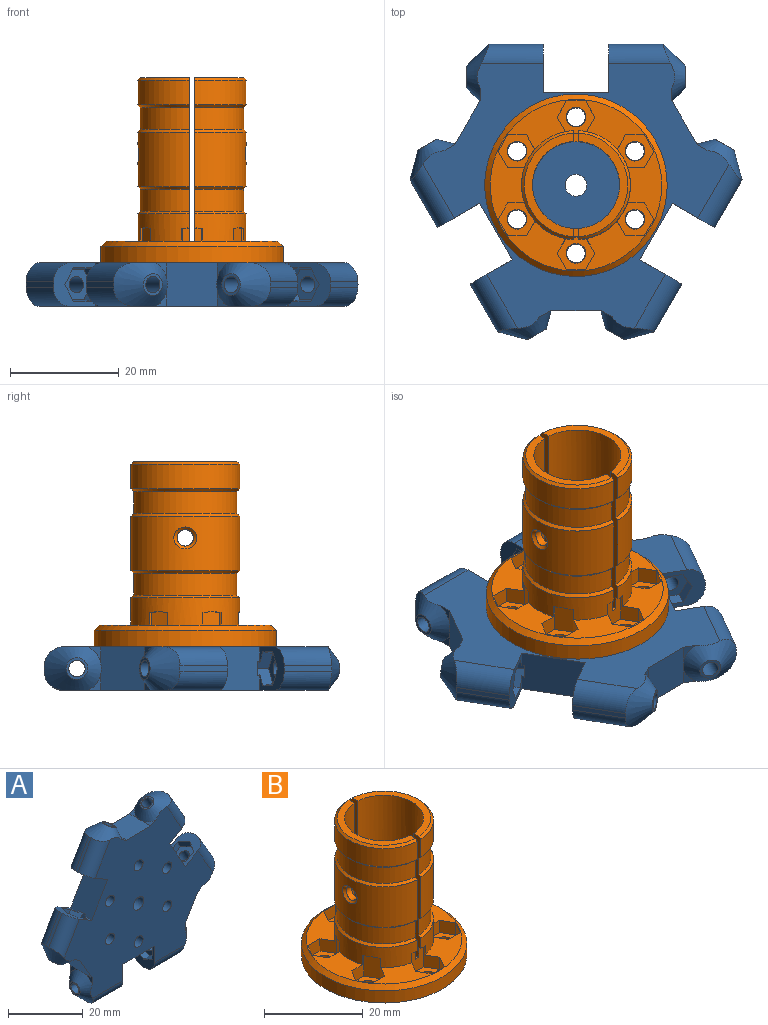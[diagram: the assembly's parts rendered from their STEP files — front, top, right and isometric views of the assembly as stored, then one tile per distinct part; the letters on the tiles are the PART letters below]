
ASSEMBLY  parts=2 mates=1
PART A: 119 faces, bbox 62.3x12.1x54.3 mm
  f0: cylinder r=2mm len=4mm, axis (0,-1,0), area 50.3mm2, adj f93,f118
  f1: cylinder r=1.7mm len=8mm, axis (0,-1,0), area 85.5mm2, adj f92,f118
  f2: cylinder r=1.7mm len=8mm, axis (0,-1,0), area 85.5mm2, adj f92,f118
  f3: cylinder r=1.7mm len=8mm, axis (0,-1,0), area 85.5mm2, adj f92,f118
  f4: cylinder r=1.7mm len=8mm, axis (0,-1,0), area 85.5mm2, adj f92,f118
  f5: cylinder r=1.7mm len=8mm, axis (0,-1,0), area 85.5mm2, adj f92,f118
  f6: cylinder r=1.7mm len=8mm, axis (0,-1,0), area 85.5mm2, adj f92,f118
  f7: cone r=6.1mm half-angle=45deg, axis (-0.5,0,-0.87), area 85.6mm2, adj f82,f83,f84,f86,f92,f114,f115,f116
  f8: cone r=6.07mm half-angle=45deg, axis (0.5,0,-0.87), area 85.6mm2, adj f78,f79,f80,f81,f92,f112,f113,f114
  f9: cone r=6.1mm half-angle=45deg, axis (-0.5,0,0.87), area 85.6mm2, adj f60,f61,f62,f64,f92,f106,f107,f108
  f10: cone r=6.07mm half-angle=45deg, axis (-1,0,0), area 85.6mm2, adj f56,f57,f58,f59,f92,f104,f105,f106
  f11: cone r=6.1mm half-angle=45deg, axis (1,0,0), area 85.6mm2, adj f37,f39,f40,f42,f92,f98,f99,f100
  f12: cone r=6.07mm half-angle=45deg, axis (0.5,0,0.87), area 85.6mm2, adj f34,f35,f36,f38,f92,f96,f97,f98
  f13: cylinder r=8mm len=16mm, axis (0,1,0), area 201.1mm2, adj f92,f93
  f14: cylinder r=1.5mm len=11.98mm, axis (-0.5,0,-0.87), area 114mm2, adj f25,f83
  f15: cylinder r=1.5mm len=11.98mm, axis (0.5,0,-0.87), area 114mm2, adj f24,f80
  f16: cylinder r=1.5mm len=11.98mm, axis (-0.5,0,0.87), area 114mm2, adj f23,f61
  f17: cylinder r=1.5mm len=12.1mm, axis (-1,0,0), area 114mm2, adj f22,f58
  f18: cylinder r=1.5mm len=12.1mm, axis (1,0,0), area 114mm2, adj f21,f39
  f19: cylinder r=1.5mm len=11.98mm, axis (0.5,0,0.87), area 114mm2, adj f20,f36
  f20: plane 5.5x5.5mm, normal (0.5,0,0.87), area 19.1mm2, adj f19,f28,f29,f30,f31,f32,f33
  f21: plane 6.35x5.5mm, normal (1,0,0), area 19.1mm2, adj f18,f41,f43,f44,f45,f46,f47
  f22: plane 6.35x5.5mm, normal (-1,0,0), area 19.1mm2, adj f17,f50,f51,f52,f53,f54,f55
  f23: plane 5.5x5.5mm, normal (-0.5,0,0.87), area 19.1mm2, adj f16,f63,f65,f66,f67,f68,f69
  f24: plane 5.5x5.5mm, normal (0.5,0,-0.87), area 19.1mm2, adj f15,f72,f73,f74,f75,f76,f77
  f25: plane 5.5x5.5mm, normal (-0.5,0,-0.87), area 19.1mm2, adj f14,f85,f87,f88,f89,f90,f91
  f26: plane 2.65x0.66mm, normal (0.5,0,0.87), area 1mm2, adj f85,f87,f94
  f27: plane 2.65x0.66mm, normal (-0.5,0,-0.87), area 1mm2, adj f28,f33,f94
  f28: plane 3.1x3.07mm, normal (-0.65,0.49,0.58), area 7.6mm2, adj f20,f27,f29,f33,f94,f95
  f29: plane 3.93x3.42mm, normal (0.09,0.98,0.15), area 6.9mm2, adj f20,f28,f30,f95
  f30: plane 3.1x2.73mm, normal (0.83,0.49,-0.28), area 6.9mm2, adj f20,f29,f31,f95
  f31: plane 3.1x2.73mm, normal (0.83,-0.49,-0.28), area 6.9mm2, adj f20,f30,f32,f95
  f32: plane 3.93x3.42mm, normal (0.09,-0.98,0.15), area 6.9mm2, adj f20,f31,f33,f95
  f33: plane 3.1x3.07mm, normal (-0.65,-0.49,0.58), area 7.6mm2, adj f20,f27,f28,f32,f94,f95
  f34: cylinder r=3.5mm len=11.61mm, axis (-0.5,0,-0.87), area 59mm2, adj f12,f35,f92,f95
  f35: plane 8.76x5.06mm, normal (-0.87,0,0.5), area 10.1mm2, adj f12,f34,f95,f96
  f36: plane 4x3.46mm, normal (-0.5,0,-0.87), area 5.5mm2, adj f12,f19
  f37: plane 2.9x2.3mm, normal (-1,0,0), area 2.3mm2, adj f11,f92,f98
  f38: plane 2.9x1.99mm, normal (-0.5,0,-0.87), area 2.3mm2, adj f12,f92,f98
  f39: plane 4x4mm, normal (-1,0,0), area 5.5mm2, adj f11,f18
  f40: plane 10.11x1.01mm, normal (0,0,-1), area 10.1mm2, adj f11,f42,f100,f101
  f41: plane 3.1x2.5mm, normal (0.17,0.49,-0.85), area 7.6mm2, adj f21,f43,f47,f48,f101,f102
  f42: cylinder r=3.5mm len=11.38mm, axis (1,0,0), area 59mm2, adj f11,f40,f92,f101
  f43: plane 3.1x2.5mm, normal (0.17,-0.49,-0.85), area 7.6mm2, adj f21,f41,f44,f48,f101,f102
  f44: plane 3.58x2mm, normal (0.17,-0.98,0), area 6.9mm2, adj f21,f43,f45,f101
  f45: plane 3.1x2mm, normal (0.17,-0.49,0.85), area 6.9mm2, adj f21,f44,f46,f101
  f46: plane 3.1x2mm, normal (0.17,0.49,0.85), area 6.9mm2, adj f21,f45,f47,f101
  f47: plane 3.58x2mm, normal (0.17,0.98,0), area 6.9mm2, adj f21,f41,f46,f101
  f48: plane 2.65x0.76mm, normal (-1,0,0), area 1mm2, adj f41,f43,f102
  f49: plane 2.65x0.76mm, normal (1,0,0), area 1mm2, adj f50,f55,f102
  f50: plane 3.1x2.5mm, normal (-0.17,0.49,-0.85), area 7.6mm2, adj f22,f49,f51,f55,f102,f103
  f51: plane 3.58x2mm, normal (-0.17,0.98,0), area 6.9mm2, adj f22,f50,f52,f103
  f52: plane 3.1x2mm, normal (-0.17,0.49,0.85), area 6.9mm2, adj f22,f51,f53,f103
  f53: plane 3.1x2mm, normal (-0.17,-0.49,0.85), area 6.9mm2, adj f22,f52,f54,f103
  f54: plane 3.58x2mm, normal (-0.17,-0.98,0), area 6.9mm2, adj f22,f53,f55,f103
  f55: plane 3.1x2.5mm, normal (-0.17,-0.49,-0.85), area 7.6mm2, adj f22,f49,f50,f54,f102,f103
  f56: cylinder r=3.5mm len=11.38mm, axis (1,0,0), area 59mm2, adj f10,f57,f92,f103
  f57: plane 10.11x1.01mm, normal (0,0,-1), area 10.1mm2, adj f10,f56,f103,f104
  f58: plane 4x4mm, normal (1,0,0), area 5.5mm2, adj f10,f17
  f59: plane 2.9x2.3mm, normal (1,0,0), area 2.3mm2, adj f10,f92,f106
  f60: plane 2.9x1.99mm, normal (0.5,0,-0.87), area 2.3mm2, adj f9,f92,f106
  f61: plane 4x3.46mm, normal (0.5,0,-0.87), area 5.5mm2, adj f9,f16
  f62: plane 8.76x5.06mm, normal (0.87,0,0.5), area 10.1mm2, adj f9,f64,f108,f109
  f63: plane 3.1x3.07mm, normal (0.65,0.49,0.58), area 7.6mm2, adj f23,f65,f69,f70,f109,f110
  f64: cylinder r=3.5mm len=11.61mm, axis (-0.5,0,0.87), area 59mm2, adj f9,f62,f92,f109
  f65: plane 3.1x3.07mm, normal (0.65,-0.49,0.58), area 7.6mm2, adj f23,f63,f66,f70,f109,f110
  f66: plane 3.93x3.42mm, normal (-0.09,-0.98,0.15), area 6.9mm2, adj f23,f65,f67,f109
  f67: plane 3.1x2.73mm, normal (-0.83,-0.49,-0.28), area 6.9mm2, adj f23,f66,f68,f109
  f68: plane 3.1x2.73mm, normal (-0.83,0.49,-0.28), area 6.9mm2, adj f23,f67,f69,f109
  f69: plane 3.93x3.42mm, normal (-0.09,0.98,0.15), area 6.9mm2, adj f23,f63,f68,f109
  f70: plane 2.65x0.66mm, normal (0.5,0,-0.87), area 1mm2, adj f63,f65,f110
  f71: plane 2.65x0.66mm, normal (-0.5,0,0.87), area 1mm2, adj f72,f77,f110
  f72: plane 3.21x3.1mm, normal (0.83,0.49,0.28), area 7.6mm2, adj f24,f71,f73,f77,f110,f111
  f73: plane 3.93x3.42mm, normal (0.09,0.98,-0.15), area 6.9mm2, adj f24,f72,f74,f111
  f74: plane 3.1x2.73mm, normal (-0.65,0.49,-0.58), area 6.9mm2, adj f24,f73,f75,f111
  f75: plane 3.1x2.73mm, normal (-0.65,-0.49,-0.58), area 6.9mm2, adj f24,f74,f76,f111
  f76: plane 3.93x3.42mm, normal (0.09,-0.98,-0.15), area 6.9mm2, adj f24,f75,f77,f111
  f77: plane 3.21x3.1mm, normal (0.83,-0.49,0.28), area 7.6mm2, adj f24,f71,f72,f76,f110,f111
  f78: cylinder r=3.5mm len=11.61mm, axis (-0.5,0,0.87), area 59mm2, adj f8,f79,f92,f111
  f79: plane 8.76x5.06mm, normal (0.87,0,0.5), area 10.1mm2, adj f8,f78,f111,f112
  f80: plane 4x3.46mm, normal (-0.5,0,0.87), area 5.5mm2, adj f8,f15
  f81: plane 2.9x1.99mm, normal (-0.5,0,0.87), area 2.3mm2, adj f8,f92,f114
  f82: plane 2.9x1.99mm, normal (0.5,0,0.87), area 2.3mm2, adj f7,f92,f114
  f83: plane 4x3.46mm, normal (0.5,0,0.87), area 5.5mm2, adj f7,f14
  f84: plane 8.76x5.06mm, normal (-0.87,0,0.5), area 10.1mm2, adj f7,f86,f116,f117
  f85: plane 3.21x3.1mm, normal (-0.83,0.49,0.28), area 7.6mm2, adj f25,f26,f87,f91,f94,f117
  f86: cylinder r=3.5mm len=11.61mm, axis (-0.5,0,-0.87), area 59mm2, adj f7,f84,f92,f117
  f87: plane 3.21x3.1mm, normal (-0.83,-0.49,0.28), area 7.6mm2, adj f25,f26,f85,f88,f94,f117
  f88: plane 3.93x3.42mm, normal (-0.09,-0.98,-0.15), area 6.9mm2, adj f25,f87,f89,f117
  f89: plane 3.1x2.73mm, normal (0.65,-0.49,-0.58), area 6.9mm2, adj f25,f88,f90,f117
  f90: plane 3.1x2.73mm, normal (0.65,0.49,-0.58), area 6.9mm2, adj f25,f89,f91,f117
  f91: plane 3.93x3.42mm, normal (-0.09,0.98,-0.15), area 6.9mm2, adj f25,f85,f90,f117
  f92: plane 56.17x48.64mm, normal (0,1,0), area 1422.3mm2, adj f1,f2,f3,f4,f5,f6,f7,f8
  f93: plane 16x16mm, normal (0,1,0), area 188.5mm2, adj f0,f13
  f94: plane 10.39x8mm, normal (-0.87,0,0.5), area 93.5mm2, adj f26,f27,f28,f33,f85,f87,f92,f95
  f95: plane 8x7.73mm, normal (0.5,0,0.87), area 33.5mm2, adj f28,f29,f30,f31,f32,f33,f34,f35
  f96: cylinder r=3.5mm len=11.61mm, axis (-0.5,0,-0.87), area 59mm2, adj f12,f35,f95,f118
  f97: plane 2.9x1.99mm, normal (-0.5,0,-0.87), area 2.3mm2, adj f12,f98,f118
  f98: plane 8.09x8.04mm, normal (-0.87,0,-0.5), area 74.1mm2, adj f11,f12,f37,f38,f92,f97,f99,f118
  f99: plane 2.9x2.3mm, normal (-1,0,0), area 2.3mm2, adj f11,f98,f118
  f100: cylinder r=3.5mm len=11.38mm, axis (1,0,0), area 59mm2, adj f11,f40,f101,f118
  f101: plane 8.92x8mm, normal (1,0,0), area 33.5mm2, adj f40,f41,f42,f43,f44,f45,f46,f47
  f102: plane 12x8mm, normal (0,0,-1), area 93.5mm2, adj f41,f43,f48,f49,f50,f55,f92,f101
  f103: plane 8.92x8mm, normal (-1,0,0), area 33.5mm2, adj f50,f51,f52,f53,f54,f55,f56,f57
  f104: cylinder r=3.5mm len=11.38mm, axis (1,0,0), area 59mm2, adj f10,f57,f103,f118
  f105: plane 2.9x2.3mm, normal (1,0,0), area 2.3mm2, adj f10,f106,f118
  f106: plane 8.09x8.04mm, normal (0.87,0,-0.5), area 74.1mm2, adj f9,f10,f59,f60,f92,f105,f107,f118
  f107: plane 2.9x1.99mm, normal (0.5,0,-0.87), area 2.3mm2, adj f9,f106,f118
  f108: cylinder r=3.5mm len=11.61mm, axis (-0.5,0,0.87), area 59mm2, adj f9,f62,f109,f118
  f109: plane 8x7.73mm, normal (-0.5,0,0.87), area 33.5mm2, adj f62,f63,f64,f65,f66,f67,f68,f69
  f110: plane 10.39x8mm, normal (0.87,0,0.5), area 93.5mm2, adj f63,f65,f70,f71,f72,f77,f92,f109
  f111: plane 8x7.73mm, normal (0.5,0,-0.87), area 33.5mm2, adj f72,f73,f74,f75,f76,f77,f78,f79
  f112: cylinder r=3.5mm len=11.61mm, axis (-0.5,0,0.87), area 59mm2, adj f8,f79,f111,f118
  f113: plane 2.9x1.99mm, normal (-0.5,0,0.87), area 2.3mm2, adj f8,f114,f118
  f114: plane 9.33x8.04mm, normal (0,0,1), area 74.1mm2, adj f7,f8,f81,f82,f92,f113,f115,f118
  f115: plane 2.9x1.99mm, normal (0.5,0,0.87), area 2.3mm2, adj f7,f114,f118
  f116: cylinder r=3.5mm len=11.61mm, axis (-0.5,0,-0.87), area 59mm2, adj f7,f84,f117,f118
  f117: plane 8x7.73mm, normal (-0.5,0,-0.87), area 33.5mm2, adj f84,f85,f86,f87,f88,f89,f90,f91
  f118: plane 56.17x48.64mm, normal (0,-1,0), area 1610.8mm2, adj f0,f1,f2,f3,f4,f5,f6,f7
PART B: 105 faces, bbox 33.5x33.5x34 mm
  f0: cylinder r=8mm len=34mm, axis (0,0,1), area 1634.8mm2, adj f6,f7,f8,f11,f12,f14,f16,f25
  f1: cylinder r=10mm len=19.98mm, axis (0,0,-1), area 290.9mm2, adj f8,f11,f29,f31,f94
  f2: cylinder r=10mm len=19.98mm, axis (0,0,-1), area 290.9mm2, adj f7,f12,f33,f37,f93
  f3: plane 31.5x31.5mm, normal (0,0,1), area 287.8mm2, adj f4,f5,f17,f18,f19,f21,f22,f39
  f4: cylinder r=10mm len=19.98mm, axis (0,0,-1), area 130.3mm2, adj f3,f8,f11,f13,f32,f56,f62,f64
  f5: cylinder r=10mm len=19.98mm, axis (0,0,-1), area 130.3mm2, adj f3,f7,f12,f24,f36,f39,f40,f46
  f6: plane 1.52x1mm, normal (0,0,1), area 1.5mm2, adj f0,f7,f8,f57
  f7: plane 30x2mm, normal (1,0,0), area 54.2mm2, adj f0,f2,f5,f6,f9,f14,f33,f34
  f8: plane 30x2mm, normal (-1,0,0), area 54.2mm2, adj f0,f1,f4,f6,f10,f25,f27,f28
  f9: cylinder r=10mm len=19.98mm, axis (0,0,-1), area 136.9mm2, adj f7,f12,f34,f95
  f10: cylinder r=10mm len=19.98mm, axis (0,0,-1), area 136.9mm2, adj f8,f11,f28,f96
  f11: plane 30x2mm, normal (-1,0,0), area 55.3mm2, adj f0,f1,f4,f10,f13,f25,f26,f27
  f12: plane 30x2mm, normal (1,0,0), area 55.3mm2, adj f0,f2,f5,f9,f14,f24,f26,f33
  f13: plane 1.41x0.49mm, normal (0,0,-1), area 0.6mm2, adj f4,f11,f20,f21
  f14: plane 18.97x9mm, normal (0,0,1), area 39.7mm2, adj f0,f7,f12,f95
  f15: cylinder r=16.75mm len=33.5mm, axis (0,0,-1), area 315.7mm2, adj f16,f90
  f16: plane 33.5x33.5mm, normal (0,0,-1), area 619.3mm2, adj f0,f15,f74,f75,f76,f77,f78,f79
  f17: plane 3.46x3mm, normal (0,-1,0), area 10.4mm2, adj f3,f18,f22,f23
  f18: plane 3x3mm, normal (0.87,-0.5,0), area 10.4mm2, adj f3,f17,f19,f23
  f19: plane 3x3mm, normal (0.87,0.5,0), area 10.4mm2, adj f3,f18,f20,f23,f24
  f20: plane 3.46x3mm, normal (0,1,0), area 10.4mm2, adj f13,f19,f21,f23,f24,f26
  f21: plane 3x3mm, normal (-0.87,0.5,0), area 10.4mm2, adj f3,f13,f20,f22,f23
  f22: plane 3x3mm, normal (-0.87,-0.5,0), area 10.4mm2, adj f3,f17,f21,f23
  f23: plane 6.93x6mm, normal (0,0,1), area 21mm2, adj f17,f18,f19,f20,f21,f22,f79
  f24: plane 1.41x0.49mm, normal (0,0,-1), area 0.6mm2, adj f5,f12,f19,f20
  f25: plane 18.97x9mm, normal (0,0,1), area 39.7mm2, adj f0,f8,f11,f96
  f26: plane 1.52x1mm, normal (0,0,1), area 1.5mm2, adj f0,f11,f12,f20
  f27: cylinder r=9.49mm len=18.95mm, axis (0,0,1), area 115.2mm2, adj f8,f11,f102,f103
  f28: plane 19.98x9.5mm, normal (0,0,-1), area 0.4mm2, adj f8,f10,f11,f102
  f29: plane 19.98x9.5mm, normal (0,0,1), area 0.4mm2, adj f1,f8,f11,f103
  f30: cylinder r=9.49mm len=18.95mm, axis (0,0,1), area 115.2mm2, adj f8,f11,f99,f100
  f31: plane 19.98x9.5mm, normal (0,0,-1), area 0.4mm2, adj f1,f8,f11,f99
  f32: plane 19.98x9.5mm, normal (0,0,1), area 0.4mm2, adj f4,f8,f11,f100
  f33: plane 19.98x9.5mm, normal (0,0,1), area 0.4mm2, adj f2,f7,f12,f104
  f34: plane 19.98x9.5mm, normal (0,0,-1), area 0.4mm2, adj f7,f9,f12,f101
  f35: cylinder r=9.49mm len=18.95mm, axis (0,0,1), area 115.2mm2, adj f7,f12,f101,f104
  f36: plane 19.98x9.5mm, normal (0,0,1), area 0.4mm2, adj f5,f7,f12,f97
  f37: plane 19.98x9.5mm, normal (0,0,-1), area 0.4mm2, adj f2,f7,f12,f98
  f38: cylinder r=9.49mm len=18.95mm, axis (0,0,1), area 115.2mm2, adj f7,f12,f97,f98
  f39: plane 5.3x3.46mm, normal (0,1,0), area 11.2mm2, adj f3,f5,f42,f43,f45,f80
  f40: plane 5.3x3mm, normal (-0.87,-0.5,0), area 11.2mm2, adj f3,f5,f43,f44,f45,f81
  f41: plane 3x3mm, normal (0.87,-0.5,0), area 10.4mm2, adj f3,f42,f44,f45
  f42: plane 3x3mm, normal (0.87,0.5,0), area 10.4mm2, adj f3,f39,f41,f45
  f43: plane 5.45x3mm, normal (-0.87,0.5,0), area 18.6mm2, adj f39,f40,f45,f80,f81
  f44: plane 3.46x3mm, normal (0,-1,0), area 10.4mm2, adj f3,f40,f41,f45
  f45: plane 6.93x6mm, normal (0,0,1), area 21mm2, adj f39,f40,f41,f42,f43,f44,f78
  f46: plane 5.3x3mm, normal (-0.87,0.5,0), area 11.2mm2, adj f3,f5,f49,f50,f52,f82
  f47: plane 5.3x3.46mm, normal (0,-1,0), area 11.2mm2, adj f3,f5,f50,f51,f52,f83
  f48: plane 3x3mm, normal (0.87,0.5,0), area 10.4mm2, adj f3,f49,f51,f52
  f49: plane 3.46x3mm, normal (0,1,0), area 10.4mm2, adj f3,f46,f48,f52
  f50: plane 5.45x3mm, normal (-0.87,-0.5,0), area 18.6mm2, adj f46,f47,f52,f82,f83
  f51: plane 3x3mm, normal (0.87,-0.5,0), area 10.4mm2, adj f3,f47,f48,f52
  f52: plane 6.93x6mm, normal (0,0,1), area 21mm2, adj f46,f47,f48,f49,f50,f51,f77
  f53: plane 5.3x3mm, normal (0.87,-0.5,0), area 11.2mm2, adj f3,f5,f57,f58,f59,f84
  f54: plane 3.46x3mm, normal (0,1,0), area 10.4mm2, adj f3,f55,f58,f59
  f55: plane 3x3mm, normal (-0.87,0.5,0), area 10.4mm2, adj f3,f54,f56,f59
  f56: plane 5.3x3mm, normal (-0.87,-0.5,0), area 11.2mm2, adj f3,f4,f55,f57,f59,f85
  f57: plane 5.41x3.46mm, normal (0,-1,0), area 16.2mm2, adj f6,f7,f8,f53,f56,f59,f84,f85
  f58: plane 3x3mm, normal (0.87,0.5,0), area 10.4mm2, adj f3,f53,f54,f59
  f59: plane 6.93x6mm, normal (0,0,1), area 21mm2, adj f53,f54,f55,f56,f57,f58,f76
  f60: plane 3x3mm, normal (-0.87,0.5,0), area 10.4mm2, adj f3,f61,f65,f66
  f61: plane 3x3mm, normal (-0.87,-0.5,0), area 10.4mm2, adj f3,f60,f62,f66
  f62: plane 5.3x3.46mm, normal (0,-1,0), area 11.2mm2, adj f3,f4,f61,f63,f66,f86
  f63: plane 5.45x3mm, normal (0.87,-0.5,0), area 18.6mm2, adj f62,f64,f66,f86,f87
  f64: plane 5.3x3mm, normal (0.87,0.5,0), area 11.2mm2, adj f3,f4,f63,f65,f66,f87
  f65: plane 3.46x3mm, normal (0,1,0), area 10.4mm2, adj f3,f60,f64,f66
  f66: plane 6.93x6mm, normal (0,0,1), area 21mm2, adj f60,f61,f62,f63,f64,f65,f75
  f67: plane 3x3mm, normal (-0.87,-0.5,0), area 10.4mm2, adj f3,f68,f72,f73
  f68: plane 3.46x3mm, normal (0,-1,0), area 10.4mm2, adj f3,f67,f69,f73
  f69: plane 5.3x3mm, normal (0.87,-0.5,0), area 11.2mm2, adj f3,f4,f68,f70,f73,f88
  f70: plane 5.45x3mm, normal (0.87,0.5,0), area 18.6mm2, adj f69,f71,f73,f88,f89
  f71: plane 5.3x3.46mm, normal (0,1,0), area 11.2mm2, adj f3,f4,f70,f72,f73,f89
  f72: plane 3x3mm, normal (-0.87,0.5,0), area 10.4mm2, adj f3,f67,f71,f73
  f73: plane 6.93x6mm, normal (0,0,1), area 21mm2, adj f67,f68,f69,f70,f71,f72,f74
  f74: cylinder r=1.8mm len=3.6mm, axis (0,0,-1), area 11.3mm2, adj f16,f73
  f75: cylinder r=1.8mm len=3.6mm, axis (0,0,-1), area 11.3mm2, adj f16,f66
  f76: cylinder r=1.8mm len=3.6mm, axis (0,0,-1), area 11.3mm2, adj f16,f59
  f77: cylinder r=1.8mm len=3.6mm, axis (0,0,-1), area 11.3mm2, adj f16,f52
  f78: cylinder r=1.8mm len=3.6mm, axis (0,0,-1), area 11.3mm2, adj f16,f45
  f79: cylinder r=1.8mm len=3.6mm, axis (0,0,-1), area 11.3mm2, adj f16,f23
  f80: plane 1.75x1.23mm, normal (0,0.1,-1), area 0.8mm2, adj f5,f39,f43,f81
  f81: plane 1.82x1.3mm, normal (-0.09,-0.05,-1), area 0.8mm2, adj f5,f40,f43,f80
  f82: plane 1.82x1.3mm, normal (-0.09,0.05,-1), area 0.8mm2, adj f5,f46,f50,f83
  f83: plane 1.75x1.23mm, normal (0,-0.1,-1), area 0.8mm2, adj f5,f47,f50,f82
  f84: plane 1.42x0.49mm, normal (0.09,-0.05,-1), area 0.6mm2, adj f5,f7,f53,f57
  f85: plane 1.42x0.49mm, normal (-0.09,-0.05,-1), area 0.6mm2, adj f4,f8,f56,f57
  f86: plane 1.75x1.23mm, normal (0,-0.1,-1), area 0.8mm2, adj f4,f62,f63,f87
  f87: plane 1.82x1.3mm, normal (0.09,0.05,-1), area 0.8mm2, adj f4,f63,f64,f86
  f88: plane 1.82x1.3mm, normal (0.09,-0.05,-1), area 0.8mm2, adj f4,f69,f70,f89
  f89: plane 1.75x1.23mm, normal (0,0.1,-1), area 0.8mm2, adj f4,f70,f71,f88
  f90: cone r=15.75mm half-angle=45deg, axis (0,0,-1), area 144.4mm2, adj f3,f15
  f91: cylinder r=1.5mm len=3mm, axis (1,0,0), area 14.1mm2, adj f0,f93
  f92: cylinder r=1.5mm len=3mm, axis (-1,0,0), area 14.1mm2, adj f0,f94
  f93: bspline ~4.21x4mm, area 8.3mm2, adj f2,f91
  f94: bspline ~4.21x4mm, area 8.3mm2, adj f1,f92
  f95: cone r=9.5mm half-angle=45deg, axis (0,0,-1), area 21mm2, adj f7,f9,f12,f14
  f96: cone r=9.5mm half-angle=45deg, axis (0,0,-1), area 21mm2, adj f8,f10,f11,f25
  f97: cone r=9.49mm half-angle=45deg, axis (0,0,-1), area 20.9mm2, adj f7,f12,f36,f38
  f98: cone r=9.99mm half-angle=45deg, axis (0,0,1), area 20.9mm2, adj f7,f12,f37,f38
  f99: cone r=9.99mm half-angle=45deg, axis (0,0,1), area 20.9mm2, adj f8,f11,f30,f31
  f100: cone r=9.49mm half-angle=45deg, axis (0,0,-1), area 20.9mm2, adj f8,f11,f30,f32
  f101: cone r=9.99mm half-angle=45deg, axis (0,0,1), area 20.9mm2, adj f7,f12,f34,f35
  f102: cone r=9.99mm half-angle=45deg, axis (0,0,1), area 20.9mm2, adj f8,f11,f27,f28
  f103: cone r=9.49mm half-angle=45deg, axis (0,0,-1), area 20.9mm2, adj f8,f11,f27,f29
  f104: cone r=9.49mm half-angle=45deg, axis (0,0,-1), area 20.9mm2, adj f7,f12,f33,f35
PLACE A rot(axis=(1,0,0),90deg) t=(-6.78,2.16,17.2)mm
PLACE B t=(-6.78,2.16,21.2)mm
MATE fastened B.f15 <-> A.f0  axis (0,0,-1) through (-6.78,2.16,21.2)mm
